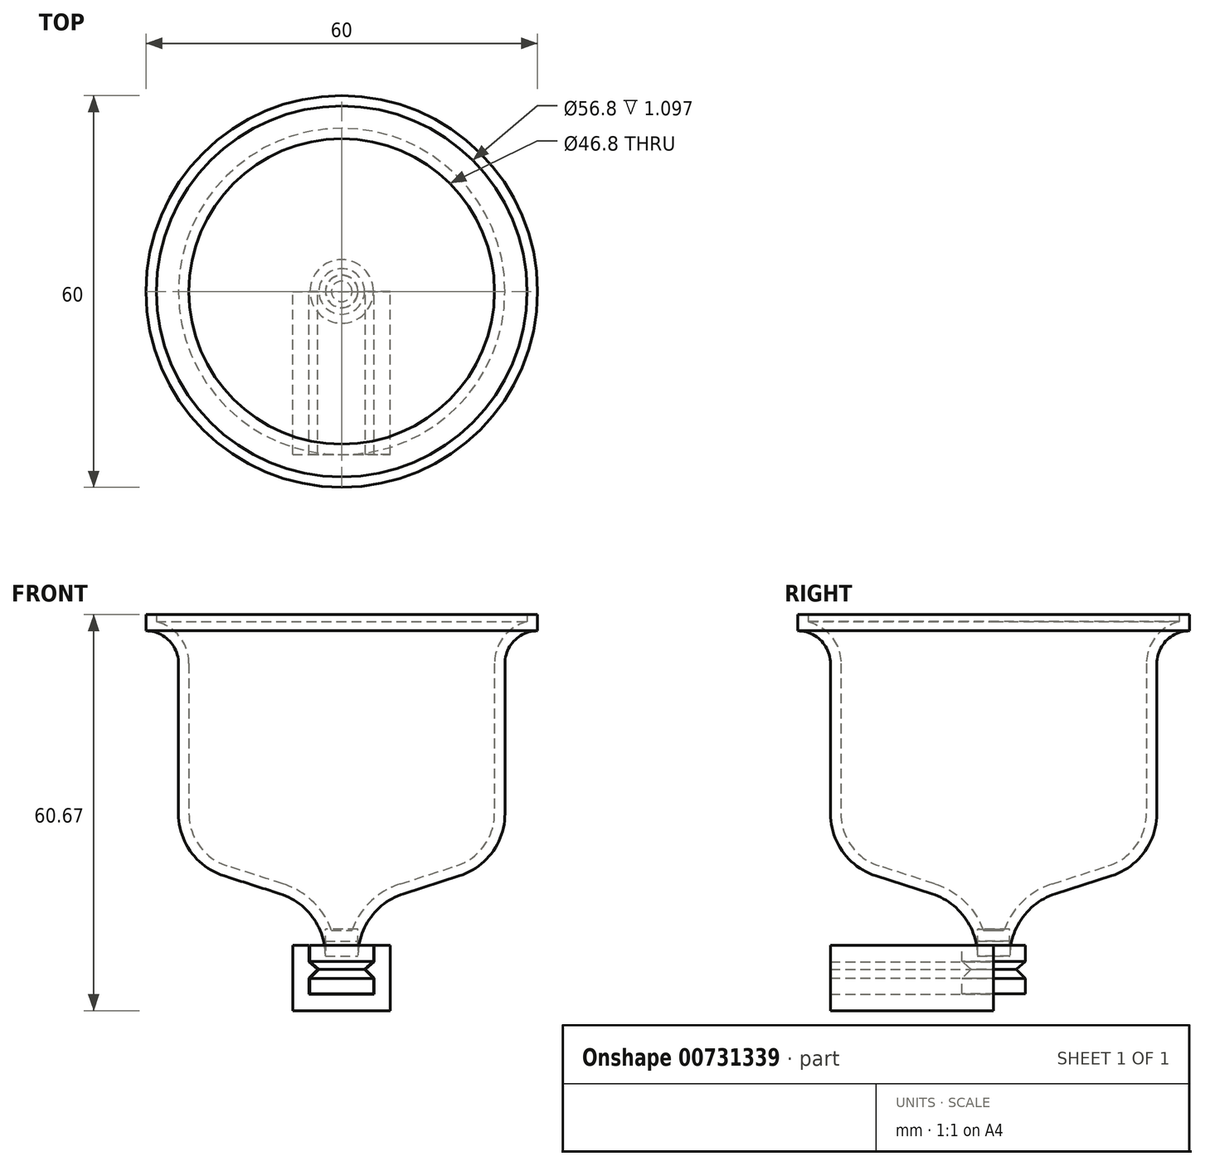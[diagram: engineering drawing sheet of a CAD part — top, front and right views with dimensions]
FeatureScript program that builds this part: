
annotation { "Feature Type Name" : "Feature", "Feature Type Description" : "" }
export const myFeature = defineFeature(function(context is Context, id is Id, definition is map)
    precondition{}
    {
        {
            var Q0;
            Q0=qCreatedBy(makeId("Front.planeOp"),FACE);
            var sketch = newSketch(context, id + "F0", { "sketchPlane" : qUnion([Q0])});
            skLineSegment(sketch, "E0.bottom", {"start": v(-7.5, 10) * mm, "end": v(-5, 10) * mm});
            skLineSegment(sketch, "E1.top", {"start": v(-5, 2.5) * mm, "end": v(0, 2.5) * mm});
            skLineSegment(sketch, "E1.left", {"start": v(-5, 5) * mm, "end": v(-5, 2.5) * mm});
            skLineSegment(sketch, "E2.right", {"start": v(-5, 10) * mm, "end": v(-5, 7.5) * mm});
            skLineSegment(sketch, "E3", {"start": v(-7.5, 10) * mm, "end": v(-7.5, 0) * mm});
            skLineSegment(sketch, "E4", {"start": v(-7.5, 0) * mm, "end": v(0, 0) * mm});
            skLineSegment(sketch, "E5.bottom", {"start": v(-2.46, 0) * mm, "end": v(0.04, 0) * mm});
            skLineSegment(sketch, "E6", {"start": v(-5, 7.5) * mm, "end": v(-3.67, 6.33) * mm});
            skLineSegment(sketch, "E7", {"start": v(-3.67, 6.33) * mm, "end": v(-5, 5) * mm});
            skLineSegment(sketch, "E8.MirrorCS", {"start": v(4.96, 7.5) * mm, "end": v(3.63, 6.33) * mm});
            skLineSegment(sketch, "E9.MirrorCS", {"start": v(7.46, 10) * mm, "end": v(4.96, 10) * mm});
            skLineSegment(sketch, "E10.MirrorCS", {"start": v(4.96, 5) * mm, "end": v(4.96, 2.5) * mm});
            skLineSegment(sketch, "E11.MirrorCS", {"start": v(4.96, 2.5) * mm, "end": v(0, 2.5) * mm});
            skLineSegment(sketch, "E12.MirrorCS", {"start": v(7.46, 10) * mm, "end": v(7.46, 0) * mm});
            skLineSegment(sketch, "E13.MirrorCS", {"start": v(7.46, 0) * mm, "end": v(0, 0) * mm});
            skLineSegment(sketch, "E14.MirrorCS", {"start": v(3.63, 6.33) * mm, "end": v(4.96, 5) * mm});
            skLineSegment(sketch, "E15.MirrorCS", {"start": v(4.96, 10) * mm, "end": v(4.96, 7.5) * mm});
            skLineSegment(sketch, "E16.MirrorCS", {"start": v(2.46, 0) * mm, "end": v(-0.04, 0) * mm});
            skLineSegment(sketch, "E17.0", {"start": v(4.86, 10) * mm, "end": v(4.86, 7.55) * mm});
            skLineSegment(sketch, "E17.1", {"start": v(4.86, 7.55) * mm, "end": v(3.49, 6.33) * mm});
            skLineSegment(sketch, "E17.2", {"start": v(3.49, 6.33) * mm, "end": v(4.86, 4.96) * mm});
            skLineSegment(sketch, "E17.3", {"start": v(4.86, 4.96) * mm, "end": v(4.86, 2.6) * mm});
            skLineSegment(sketch, "E17.4", {"start": v(4.86, 2.6) * mm, "end": v(0, 2.6) * mm});
            skLineSegment(sketch, "E17.5", {"start": v(-4.9, 2.6) * mm, "end": v(0, 2.6) * mm});
            skLineSegment(sketch, "E17.6", {"start": v(-4.9, 10) * mm, "end": v(-4.9, 7.55) * mm});
            skLineSegment(sketch, "E17.7", {"start": v(-4.9, 7.55) * mm, "end": v(-3.52, 6.33) * mm});
            skLineSegment(sketch, "E17.8", {"start": v(-3.52, 6.33) * mm, "end": v(-4.9, 4.96) * mm});
            skLineSegment(sketch, "E17.9", {"start": v(-4.9, 4.96) * mm, "end": v(-4.9, 2.6) * mm});
            skLineSegment(sketch, "E18", {"start": v(-4.9, 10) * mm, "end": v(4.86, 10) * mm});
            skLineSegment(sketch, "E19", {"start": v(-2.46, 0) * mm, "end": v(-2.46, 10) * mm});
            skLineSegment(sketch, "E20", {"start": v(-2.46, 10) * mm, "end": v(-2.46, 12.5) * mm});
            skLineSegment(sketch, "E21", {"start": v(2.46, 0) * mm, "end": v(2.46, 10) * mm});
            skLineSegment(sketch, "E22", {"start": v(2.46, 10) * mm, "end": v(2.46, 12.5) * mm});
            skLineSegment(sketch, "E23", {"start": v(2.46, 12.5) * mm, "end": v(-2.46, 12.5) * mm});
            skLineSegment(sketch, "E24", {"start": v(0, 12.5) * mm, "end": v(0, 2.6) * mm});
            skSolve(sketch);
        }
        {
            var Q0;
            {var subQ1=sQuery(id+"F0.wireOp",EDGE,"E17.4");var subQ3=sQuery(id+"F0.wireOp",EDGE,"E21");var subQ4=makeQuery(id+"F0.imprint","INTERSECT",VERTEX,{"derivedFrom":[subQ1,subQ3]});Q0=makeQuery(id+"F0.imprint","IMPRINT",FACE,{"disambiguationData":[TD([[makeQuery(id+"F0.imprint","IMPRINT",EDGE,{"disambiguationData":[TD([[subQ4,-1.0]])],"derivedFrom":subQ1}),-1.0]])]});}
            var Q1;
            {var subQ1=sQuery(id+"F0.wireOp",EDGE,"E17.0");Q1=makeQuery(id+"F0.imprint","IMPRINT",FACE,{"disambiguationData":[TD([[makeQuery(id+"F0.imprint","IMPRINT",EDGE,{"derivedFrom":subQ1}),-1.0]])]});}
            var Q2;
            {var subQ0=sQuery(id+"F0.wireOp",EDGE,"E22");Q2=makeQuery(id+"F0.imprint","IMPRINT",FACE,{"disambiguationData":[TD([[makeQuery(id+"F0.imprint","IMPRINT",EDGE,{"derivedFrom":subQ0}),1.0]])]});}
            var Q3;
            Q3=sQuery(id+"F0.wireOp",EDGE,"E24");
            revolve(context, id + "F1", {"surfaceOperationType" : NewSurfaceOperationType.NEW, "entities" : qUnion([Q0, Q1, Q2]), "axis" : qUnion([Q3]), "revolveType" : RevolveType.FULL});
        }
        {
            var Q0;
            Q0=qCreatedBy(makeId("Front.planeOp"),FACE);
            var sketch = newSketch(context, id + "F2", { "sketchPlane" : qUnion([Q0])});
            skLineSegment(sketch, "E25", {"start": v(0, 10.67) * mm, "end": v(0, 60.67) * mm});
            skLineSegment(sketch, "E26", {"start": v(0, 60.67) * mm, "end": v(-25, 60.67) * mm});
            skLineSegment(sketch, "E27", {"start": v(-2.5, 8.38) * mm, "end": v(-2.5, 10.67) * mm});
            skLineSegment(sketch, "E28", {"start": v(-9.45, 17.9) * mm, "end": v(-18.05, 20.65) * mm});
            skLineSegment(sketch, "E29", {"start": v(-25, 30.18) * mm, "end": v(-25, 53.17) * mm});
            skLineSegment(sketch, "E30", {"start": v(-2.5, 10.67) * mm, "end": v(0, 10.67) * mm});
            skPoint(sketch, "E31.visualSharp", {"position": v(-25, 22.88) * mm});
            skArc(sketch, "E31.filletArc", {"start": v(-25, 30.18) * mm, "mid": v(-23.08, 24.28) * mm, "end": v(-18.05, 20.65) * mm});
            skPoint(sketch, "E32.visualSharp", {"position": v(-2.5, 15.67) * mm});
            skArc(sketch, "E32.filletArc", {"start": v(-2.5, 8.38) * mm, "mid": v(-4.42, 14.27) * mm, "end": v(-9.45, 17.9) * mm});
            skLineSegment(sketch, "E33", {"start": v(-25, 60.67) * mm, "end": v(-30, 60.67) * mm});
            skLineSegment(sketch, "E34", {"start": v(-30, 60.67) * mm, "end": v(-30, 58.17) * mm});
            skLineSegment(sketch, "E35", {"start": v(-30, 58.17) * mm, "end": v(-30, 58.17) * mm});
            skPoint(sketch, "E36.newPointA", {"position": v(-25, 58.17) * mm});
            skArc(sketch, "E36.filletArc", {"start": v(-25, 53.17) * mm, "mid": v(-26.46, 56.7) * mm, "end": v(-30, 58.17) * mm});
            skSolve(sketch);
        }
        {
            var Q0;
            Q0=makeQuery(id+"F2.imprint","IMPRINT",FACE,{"disambiguationData":[TD([[makeQuery(id+"F2.imprint","IMPRINT",EDGE,{"derivedFrom":sQuery(id+"F2.wireOp",EDGE,"E25")}),1.0]])]});
            var Q1;
            Q1=sQuery(id+"F2.wireOp",EDGE,"E25");
            revolve(context, id + "F3", {"surfaceOperationType" : NewSurfaceOperationType.NEW, "entities" : qUnion([Q0]), "axis" : qUnion([Q1]), "revolveType" : RevolveType.FULL});
        }
        {
            var Q0;
            Q0=makeQuery(id+"F3.opRevolve","SWEPT_FACE",FACE,{"disambiguationData":[OSD([sQuery(id+"F2.wireOp",EDGE,"E26"),sQuery(id+"F2.wireOp",EDGE,"E33")])]});
            shell(context, id + "F4", {"entities" : qUnion([Q0]), "thickness" : 1.6 * mm});
        }
        {
            var Q0;
            Q0=makeQuery(id+"F0.imprint","IMPRINT",FACE,{"disambiguationData":[TD([[makeQuery(id+"F0.imprint","IMPRINT",EDGE,{"derivedFrom":sQuery(id+"F0.wireOp",EDGE,"E0.bottom")}),-1.0]])]});
            var Q1;
            {var subQ1=sQuery(id+"F0.wireOp",EDGE,"E5.bottom");Q1=makeQuery(id+"F0.imprint","IMPRINT",FACE,{"disambiguationData":[TD([[makeQuery(id+"F0.imprint","IMPRINT",EDGE,{"derivedFrom":subQ1}),1.0]])]});}
            var Q2;
            Q2=makeQuery(id+"F0.imprint","IMPRINT",FACE,{"disambiguationData":[TD([[makeQuery(id+"F0.imprint","IMPRINT",EDGE,{"derivedFrom":sQuery(id+"F0.wireOp",EDGE,"E8.MirrorCS")}),1.0]])]});
            extrude(context, id + "F5", {"entities" : qUnion([Q0, Q1, Q2]), "depth" : 25 * mm, "offsetDistance" : 25 * mm});
        }
    });
